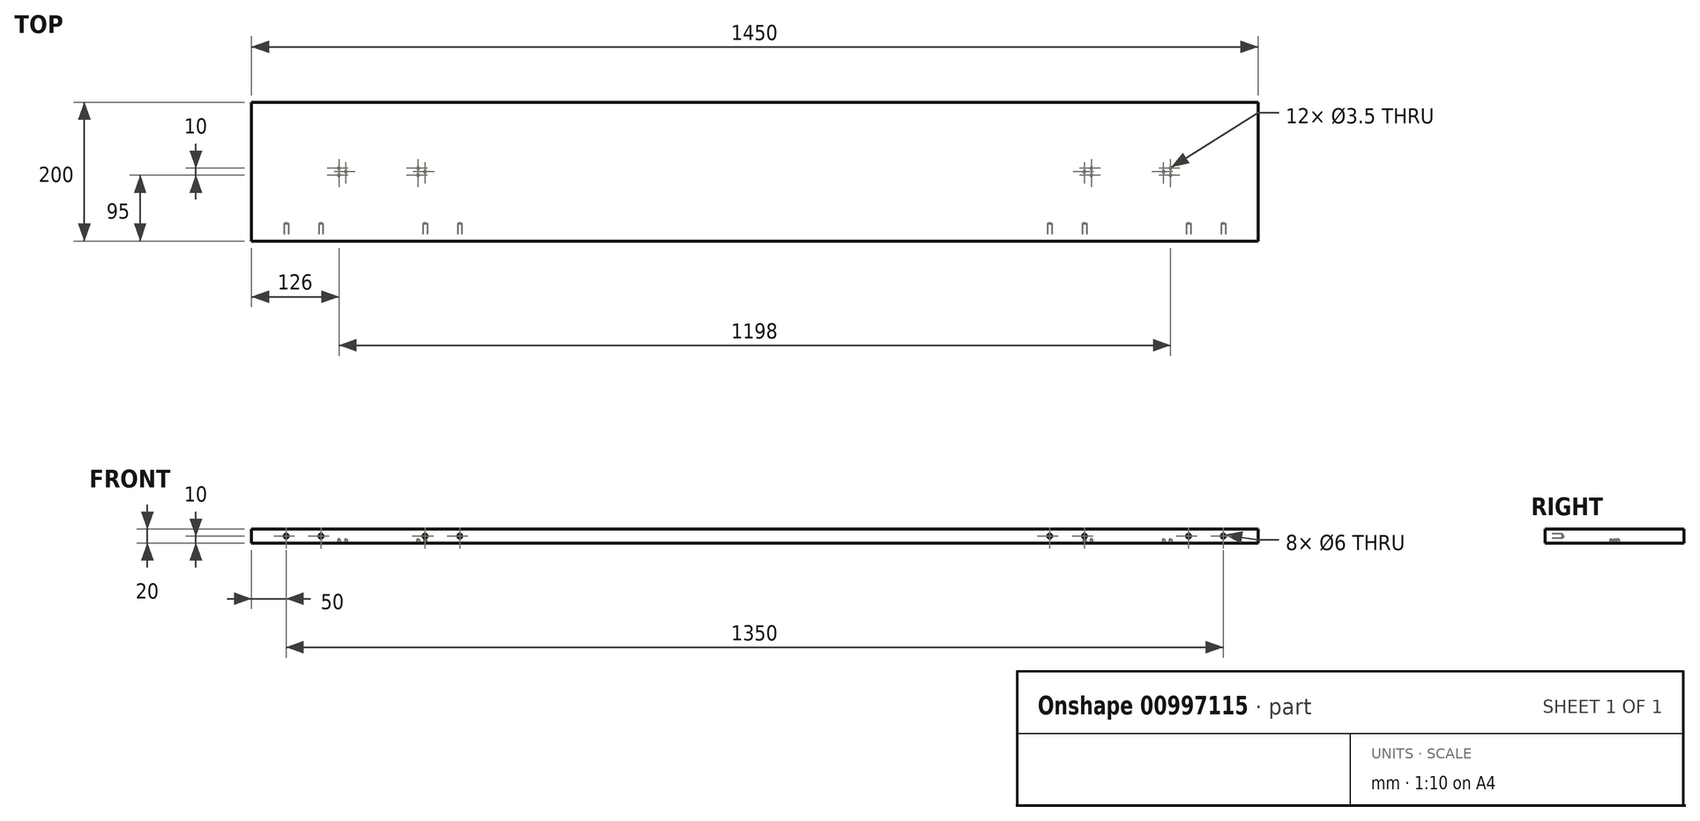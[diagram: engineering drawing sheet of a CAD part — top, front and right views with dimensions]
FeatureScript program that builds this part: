
annotation { "Feature Type Name" : "Feature", "Feature Type Description" : "" }
export const myFeature = defineFeature(function(context is Context, id is Id, definition is map)
    precondition{}
    {
        {
            var Q0;
            Q0=qCreatedBy(makeId("Top.planeOp"),FACE);
            var sketch = newSketch(context, id + "F0", { "sketchPlane" : qUnion([Q0])});
            skLineSegment(sketch, "E0.bottom", {"start": v(725, 100) * mm, "end": v(-725, 100) * mm});
            skLineSegment(sketch, "E0.top", {"start": v(725, -100) * mm, "end": v(-725, -100) * mm});
            skLineSegment(sketch, "E0.left", {"start": v(725, 100) * mm, "end": v(725, -100) * mm});
            skLineSegment(sketch, "E0.right", {"start": v(-725, 100) * mm, "end": v(-725, -100) * mm});
            skPoint(sketch, "E0.middle", {"position": v(0, 0) * mm});
            skSolve(sketch);
        }
        {
            var Q0;
            Q0 = qSketchRegion(id + "F0", true);
            extrude(context, id + "F1", {"entities" : qUnion([Q0]), "endBound" : BoundingType.SYMMETRIC, "depth" : 20 * mm, "offsetDistance" : 25 * mm});
        }
        {
            var Q0;
            Q0=makeQuery(id+"F1.opExtrude","SWEPT_FACE",FACE,{"disambiguationData":[OSD([sQuery(id+"F0.wireOp",EDGE,"E0.top")])]});
            var sketch = newSketch(context, id + "F2", { "sketchPlane" : qUnion([Q0])});
            skPoint(sketch, "E1", {"position": v(-675, 0) * mm});
            skPoint(sketch, "E2", {"position": v(-425, 0) * mm});
            skPoint(sketch, "E3", {"position": v(-475, 0) * mm});
            skPoint(sketch, "E4", {"position": v(-625, 0) * mm});
            skPoint(sketch, "E5.MirrorP", {"position": v(675, 0) * mm});
            skPoint(sketch, "E6.MirrorP", {"position": v(625, 0) * mm});
            skPoint(sketch, "E7.MirrorP", {"position": v(475, 0) * mm});
            skPoint(sketch, "E8.MirrorP", {"position": v(425, 0) * mm});
            skSolve(sketch);
        }
        {
            var Q0;
            Q0=sQuery(id+"F2.wireOp",VERTEX,"E1");
            var Q1;
            Q1=sQuery(id+"F2.wireOp",VERTEX,"E4");
            var Q2;
            Q2=sQuery(id+"F2.wireOp",VERTEX,"E3");
            var Q3;
            Q3=sQuery(id+"F2.wireOp",VERTEX,"E2");
            var Q4;
            Q4=sQuery(id+"F2.wireOp",VERTEX,"E8.MirrorP");
            var Q5;
            Q5=sQuery(id+"F2.wireOp",VERTEX,"E7.MirrorP");
            var Q6;
            Q6=sQuery(id+"F2.wireOp",VERTEX,"E6.MirrorP");
            var Q7;
            Q7=sQuery(id+"F2.wireOp",VERTEX,"E5.MirrorP");
            var Q8;
            Q8=makeQuery(id+"F1.opExtrude","SWEPT_BODY",BODY,{"disambiguationData":[OSD([sQuery(id+"F0.wireOp",EDGE,"E0.bottom"),sQuery(id+"F0.wireOp",EDGE,"E0.top"),sQuery(id+"F0.wireOp",EDGE,"E0.left"),sQuery(id+"F0.wireOp",EDGE,"E0.right")])]});
            hole(context, id + "F3", {"style" : HoleStyle.SIMPLE, "endStyle" : HoleEndStyle.BLIND, "holeDiameter" : 6 * mm, "majorDiameter" : 5 * mm, "holeDepth" : 25 * mm, "isTappedThrough" : true, "tappedDepth" : 12 * mm, "tapClearance" : 3, "locations" : qUnion([Q0, Q1, Q2, Q3, Q4, Q5, Q6, Q7]), "scope" : qUnion([Q8])});
        }
        {
            var Q0;
            Q0=makeQuery(id+"F1.opExtrude","CAP_FACE",FACE,{"disambiguationData":[OSD([sQuery(id+"F0.wireOp",EDGE,"E0.bottom"),sQuery(id+"F0.wireOp",EDGE,"E0.top"),sQuery(id+"F0.wireOp",EDGE,"E0.left"),sQuery(id+"F0.wireOp",EDGE,"E0.right")])],"isStart":true});
            var sketch = newSketch(context, id + "F4", { "sketchPlane" : qUnion([Q0])});
            skPoint(sketch, "E9", {"position": v(-599, 5) * mm});
            skPoint(sketch, "E10", {"position": v(-599, -5) * mm});
            skPoint(sketch, "E11", {"position": v(-589, 0) * mm});
            skPoint(sketch, "E12", {"position": v(-485, 5) * mm});
            skPoint(sketch, "E13", {"position": v(-485, -5) * mm});
            skPoint(sketch, "E14", {"position": v(-475, 0) * mm});
            skPoint(sketch, "E15.MirrorP", {"position": v(599, 5) * mm});
            skPoint(sketch, "E16.MirrorP", {"position": v(599, -5) * mm});
            skPoint(sketch, "E17.MirrorP", {"position": v(589, 0) * mm});
            skPoint(sketch, "E18.MirrorP", {"position": v(485, 5) * mm});
            skPoint(sketch, "E19.MirrorP", {"position": v(485, -5) * mm});
            skPoint(sketch, "E20.MirrorP", {"position": v(475, 0) * mm});
            skSolve(sketch);
        }
        {
            var Q0;
            Q0=sQuery(id+"F4.wireOp",VERTEX,"E9");
            var Q1;
            Q1=sQuery(id+"F4.wireOp",VERTEX,"E10");
            var Q2;
            Q2=sQuery(id+"F4.wireOp",VERTEX,"E11");
            var Q3;
            Q3=sQuery(id+"F4.wireOp",VERTEX,"E12");
            var Q4;
            Q4=sQuery(id+"F4.wireOp",VERTEX,"E13");
            var Q5;
            Q5=sQuery(id+"F4.wireOp",VERTEX,"E14");
            var Q6;
            Q6=makeQuery(id+"F1.opExtrude","SWEPT_BODY",BODY,{"disambiguationData":[OSD([sQuery(id+"F0.wireOp",EDGE,"E0.bottom"),sQuery(id+"F0.wireOp",EDGE,"E0.top"),sQuery(id+"F0.wireOp",EDGE,"E0.left"),sQuery(id+"F0.wireOp",EDGE,"E0.right")])]});
            hole(context, id + "F5", {"style" : HoleStyle.SIMPLE, "endStyle" : HoleEndStyle.BLIND, "holeDiameter" : 3.5 * mm, "majorDiameter" : 5 * mm, "holeDepth" : 5 * mm, "isTappedThrough" : true, "tappedDepth" : 12 * mm, "tapClearance" : 3, "locations" : qUnion([Q0, Q1, Q2, Q3, Q4, Q5]), "scope" : qUnion([Q6])});
        }
        {
            var Q0;
            Q0=sQuery(id+"F4.wireOp",VERTEX,"E20.MirrorP");
            var Q1;
            Q1=sQuery(id+"F4.wireOp",VERTEX,"E19.MirrorP");
            var Q2;
            Q2=sQuery(id+"F4.wireOp",VERTEX,"E18.MirrorP");
            var Q3;
            Q3=sQuery(id+"F4.wireOp",VERTEX,"E17.MirrorP");
            var Q4;
            Q4=sQuery(id+"F4.wireOp",VERTEX,"E15.MirrorP");
            var Q5;
            Q5=sQuery(id+"F4.wireOp",VERTEX,"E16.MirrorP");
            var Q6;
            Q6=makeQuery(id+"F1.opExtrude","SWEPT_BODY",BODY,{"disambiguationData":[OSD([sQuery(id+"F0.wireOp",EDGE,"E0.bottom"),sQuery(id+"F0.wireOp",EDGE,"E0.top"),sQuery(id+"F0.wireOp",EDGE,"E0.left"),sQuery(id+"F0.wireOp",EDGE,"E0.right")])]});
            hole(context, id + "F6", {"style" : HoleStyle.SIMPLE, "endStyle" : HoleEndStyle.BLIND, "holeDiameter" : 3.5 * mm, "majorDiameter" : 5 * mm, "holeDepth" : 5 * mm, "isTappedThrough" : true, "tappedDepth" : 12 * mm, "tapClearance" : 3, "locations" : qUnion([Q0, Q1, Q2, Q3, Q4, Q5]), "scope" : qUnion([Q6])});
        }
    });
